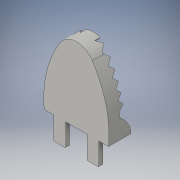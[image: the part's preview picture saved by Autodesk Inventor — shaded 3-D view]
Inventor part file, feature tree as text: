
AUTODESK INVENTOR PART (.ipt)
format: ipt  version: 2016 (Build 200138000, 138)  size: 534,016 bytes
history: native  units: in
note: dims shown in document units (in); Inventor stores cm internally (conversion verified against a paired STEP export)
features: sketch x25, extrude x24, other x12, plane x12, projected_geometry x8, fillet x4, reference x4
ambient origin geometry x8: Origin, YZ Plane, XZ Plane, XY Plane, X Axis, Y Axis, Z Axis, Center Point
bodies: Solid1 (feature_tree)
feature tree (89):
  extrude  "Extrusion1"  Depth=1.0in
  extrude  "Extrusion2"  Depth=0.3937in TaperAngle=0.0deg
  extrude  "Extrusion3"  Depth=1.0in
  extrude  "Extrusion4"  Depth=1.0in TaperAngle=0.0deg
  sketch  "Sketch5"  dims[d12=1.0in d13=0.0in d15=0.5in]
  other  "Work Point1"
  other  "Work Point2"
  other  "Work Point3"
  other  "Work Point4"
  other  "Work Point5"
  other  "Work Point6"
  other  "Work Point7"
  other  "Work Point8"
  other  "Work Point9"
  other  "Work Point10"
  other  "Work Point11"
  other  "Work Point12"
  plane  "Work Plane1"
  plane  "Work Plane2"
  plane  "Work Plane3"
  plane  "Work Plane4"
  plane  "Work Plane5"
  plane  "Work Plane6"
  sketch  "Sketch6"  dims[d16=2.3622in d18=0.45in d19=0.3937in d21=1.0in d23=0.25in]
  sketch  "Sketch7"  dims[d24=0.5in d25=0.25in]
  sketch  "Sketch8"  dims[d26=0.25in d27=0.5in d28=0.25in d29=0.25in d30=0.5in d31=0.25in]
  sketch  "Sketch9"  dims[d32=0.25in d33=0.5in d34=0.25in d35=0.25in d36=0.5in d37=0.25in]
  sketch  "Sketch10"  dims[d38=0.25in d39=0.5in d40=0.25in d44=1.0in d45=0.0in]
  sketch  "Sketch11"  dims[d46=1.0in d47=0.0in d48=1.0in d49=0.0in]
  extrude  "Extrusion5"  Depth=0.5in
  extrude  "Extrusion6"  Depth=0.3937in
  extrude  "Extrusion7"  Depth=0.25in
  extrude  "Extrusion8"  Depth=0.25in
  extrude  "Extrusion9"  Depth=0.25in
  extrude  "Extrusion10"  Depth=1.0in TaperAngle=0.0deg
  plane  "Work Plane7"
  plane  "Work Plane8"
  plane  "Work Plane9"
  plane  "Work Plane10"
  plane  "Work Plane11"
  plane  "Work Plane12"
  sketch  "Sketch13"  dims[d50=1.0in d51=0.0in d52=1.0in d53=0.0in]
  sketch  "Sketch14"  dims[d54=1.0in d55=0.0in d56=0.25in]
  sketch  "Sketch15"  dims[d57=0.5in d58=0.25in]
  sketch  "Sketch16"  dims[d59=0.25in d60=0.5in d61=0.25in d62=0.25in d63=0.5in d64=0.25in]
  sketch  "Sketch17"  dims[d65=0.25in d66=0.5in d67=0.25in d68=0.25in d69=0.5in d70=0.25in]
  sketch  "Sketch18"  dims[d71=0.25in d72=0.5in d73=0.25in d74=1.0in d75=0.0in]
  extrude  "Extrusion11"  Depth=1.0in TaperAngle=0.0deg
  extrude  "Extrusion12"  Depth=1.0in TaperAngle=0.0deg
  extrude  "Extrusion13"  Depth=0.25in
  extrude  "Extrusion14"  Depth=0.25in
  extrude  "Extrusion15"  Depth=0.25in
  extrude  "Extrusion16"  Depth=0.25in
  extrude  "Extrusion17"  Depth=1.0in TaperAngle=0.0deg
  extrude  "Extrusion18"  Depth=1.0in TaperAngle=0.0deg
  extrude  "Extrusion19"  Depth=1.0in TaperAngle=0.0deg
  extrude  "Extrusion20"  Depth=1.0in TaperAngle=0.0deg
  extrude  "Extrusion21"  Depth=0.3937in
  extrude  "Extrusion22"  Depth=0.3937in
  extrude  "Extrusion23"  Depth=0.1969in
  extrude  "Extrusion24"  Depth=0.1969in
  fillet  "Fillet1"  Radius=0.7874in
  fillet  "Fillet2"  Radius=1.2402in
  fillet  "Fillet3"  Radius=0.1969in
  fillet  "Fillet4"  Radius=0.1378in
  sketch  "Sketch1"  dims[d0=4.5in d1=1.0in]
  reference  "Reference1"
  sketch  "Sketch2"  dims[d2=0.1969in d3=0.0in d4=0.3937in d5=0.0in]
  projected_geometry  "Projected Loop1"
  sketch  "Sketch3"  dims[d6=0.9843in d7=1.0in]
  sketch  "Sketch4"  dims[d8=4.0in d9=0.0in d10=1.0in d11=0.0in]
  projected_geometry  "Projected Loop2"
  projected_geometry  "Projected Loop3"
  sketch  "Sketch19"  dims[d76=1.0in d77=0.0in d78=1.0in d79=0.0in]
  projected_geometry  "Projected Loop4"
  sketch  "Sketch20"  dims[d80=1.0in d81=0.0in d82=1.0in d83=0.0in]
  reference  "Reference2"
  sketch  "Sketch21"  dims[d84=1.0in d85=0.0in d86=1.0in d87=0.0in]
  reference  "Reference3"
  reference  "Reference4"
  sketch  "Sketch22"  dims[d88=4.0in d89=0.0in d90=0.3937in]
  sketch  "Sketch23"  dims[d91=0.3937in d92=0.0787in]
  projected_geometry  "Projected Loop5"
  projected_geometry  "Projected Loop6"
  projected_geometry  "Projected Loop7"
  sketch  "Sketch24"  dims[d93=0.0787in d94=0.1969in]
  projected_geometry  "Projected Loop8"
  sketch  "Sketch25"  dims[d95=0.7874in d96=0.1969in d97=0.7874in d98=1.2402in d99=0.0in d100=0.1969in d101=0.1378in]
  sketch  "Sketch26"  dims[d102=1.5748in d103=0.0in d104=1.5748in d105=0.0in d106=0.2953in d107=0.0in d108=0.2in d109=0.0in d110=0.0098in d111=1.1972in d112=0.6262in d113=0.0098in d114=0.15in d115=0.1in d116=0.0in d117=0.0394in d118=0.0394in d119=0.0394in d120=0.0394in]
